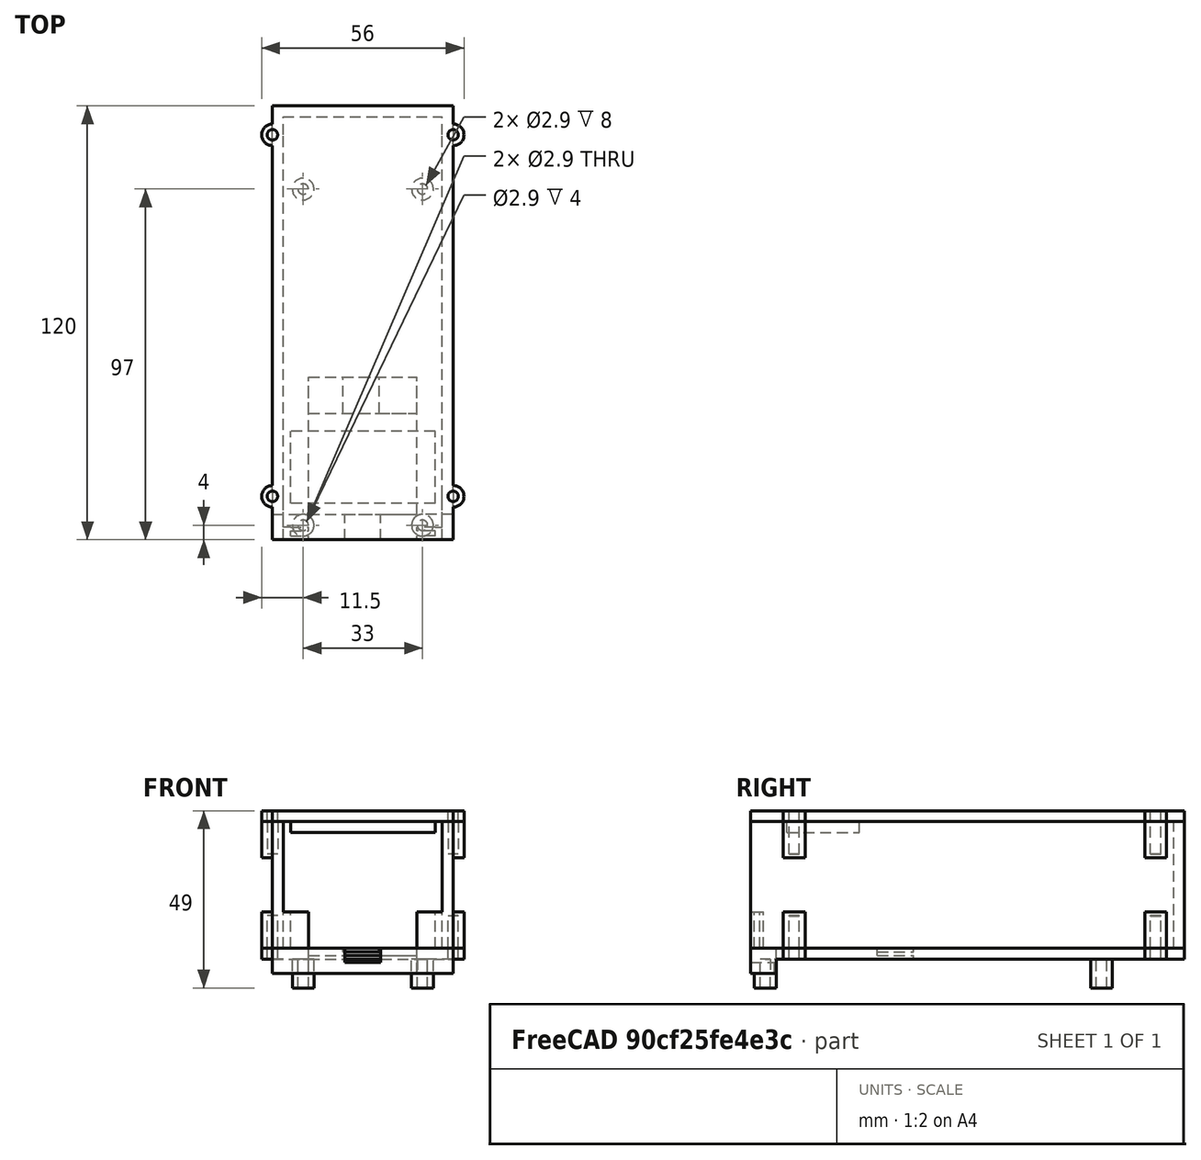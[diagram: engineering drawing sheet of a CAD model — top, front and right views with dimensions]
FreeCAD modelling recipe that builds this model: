
FCSTD DOCUMENT  (FreeCAD 0.18.4R)
Label: case
License: All rights reserved
LicenseURL: http://en.wikipedia.org/wiki/All_rights_reserved
objects: Part::FeaturePython×47, Part::Cylinder×29, Part::Box×18, Part::Mirroring×3
note: 97 computed .brp shape members not serialized (recipe doc carries the construction recipe); baked Part::Feature solids carry a one-line shape summary decoded from their .brp

FEATURE [Part::Box] Box002  label="Cube002"
  AttacherType = Attacher::AttachEngine3D
  Height = 10
  Length = 5
  Placement = pos=(0,2.5,1) rot=(0,0,1;0rad)
  Width = 1
FEATURE [Part::Mirroring] Part__Mirroring  label="Cube003 (Mirror #1)"
  Base = (0,0,0)
  Normal = (1,0,0)
FEATURE [Part::Mirroring] Part__Mirroring001  label="Cube004 (Mirror #2)"
  Base = (0,0,0)
  Normal = (1,0,0)
FEATURE [Part::Mirroring] Part__Mirroring002  label="Cube005 (Mirror #3)"
  Base = (0,0,0)
  Normal = (1,0,0)
FEATURE [Part::Box] Box007  label="Cube007"
  AttacherType = Attacher::AttachEngine3D
  Height = 3
  Length = 10
  Placement = pos=(-5,0,-2) rot=(0,0,1;0rad)
  Width = 45
FEATURE [Part::Box] Box009  label="Cube009"
  AttacherType = Attacher::AttachEngine3D
  Height = 35
  Length = 44
  Placement = pos=(-2,117,1) rot=(0,0,1;0rad)
  Width = 3
FEATURE [Part::Box] Box016  label="Floor"
  AttacherType = Attacher::AttachEngine3D
  Height = 3
  Length = 50
  Placement = pos=(-5,45,-2) rot=(0,0,1;0rad)
  Width = 75
FEATURE [Part::Box] Box018  label="Cube016"
  AttacherType = Attacher::AttachEngine3D
  Height = 1
  Length = 10
  Placement = pos=(14.5,35,0) rot=(0,0,1;0rad)
  Width = 10
FEATURE [Part::Box] Box008  label="Cube008"
  AttacherType = Attacher::AttachEngine3D
  Height = 2
  Length = 30
  Placement = pos=(5,35,-1) rot=(0,0,1;0rad)
  Width = 10
FEATURE [Part::FeaturePython] Cutout005  # WARN: FeaturePython — macro-defined, semantics opaque (R4)
  Base = -> Box008
  Tolerance = 0
  Tool = -> Box018
FEATURE [Part::Box] Box  label="Cube"
  AttacherType = Attacher::AttachEngine3D
  Height = 10
  Length = 5
  Placement = pos=(0,0,1) rot=(0,0,1;0rad)
  Width = 1
FEATURE [Part::Box] Box001  label="Cube001"
  AttacherType = Attacher::AttachEngine3D
  Height = 10
  Length = 3.5
  Placement = pos=(-2e-16,0,1) rot=(0,0,1;1.5708rad)
  Width = 2
FEATURE [Part::Box] Box010  label="Cube010"
  AttacherType = Attacher::AttachEngine3D
  Height = 35
  Length = 3
  Placement = pos=(-5,0,1) rot=(0,0,1;0rad)
  Width = 120
FEATURE [Part::Box] Box020  label="Cube018"
  AttacherType = Attacher::AttachEngine3D
  Height = 3
  Length = 10
  Placement = pos=(45,-1e-14,34) rot=(0,0,1;1.5708rad)
  Width = 50
FEATURE [Part::Box] Box021  label="Cube019"
  AttacherType = Attacher::AttachEngine3D
  Height = 3
  Length = 20
  Placement = pos=(45,10,34) rot=(0,0,1;1.5708rad)
  Width = 50
FEATURE [Part::Box] Box022  label="Cube020"
  AttacherType = Attacher::AttachEngine3D
  Height = 3
  Length = 20
  Placement = pos=(40,10,31) rot=(0,0,1;1.5708rad)
  Width = 40
FEATURE [Part::Box] Box023  label="Cube021"
  AttacherType = Attacher::AttachEngine3D
  Height = 3
  Length = 90
  Placement = pos=(45,30,34) rot=(0,0,1;1.5708rad)
  Width = 50
FEATURE [Part::FeaturePython] Connect  # WARN: FeaturePython — macro-defined, semantics opaque (R4)
  Objects = -> [Part__Mirroring,Part__Mirroring002,Part__Mirroring001]
  Placement = pos=(40,0,1) rot=(0,0,1;0rad)
  Tolerance = 0
FEATURE [Part::Box] Box019  label="Cube017"
  AttacherType = Attacher::AttachEngine3D
  Height = 35
  Length = 3
  Placement = pos=(42,0,1) rot=(0,0,1;0rad)
  Width = 120
FEATURE [Part::Box] Box031  label="Cube028"
  AttacherType = Attacher::AttachEngine3D
  Height = 7
  Length = 30
  Placement = pos=(5,0,-6) rot=(0,0,1;0rad)
  Width = 7
FEATURE [Part::Box] Box032  label="Cube029"
  AttacherType = Attacher::AttachEngine3D
  Height = 4
  Length = 10
  Placement = pos=(15,0,-3) rot=(0,0,1;0rad)
  Width = 7
FEATURE [Part::Cylinder] Cylinder036  label="outer016"
  Angle = 360
  AttacherType = Attacher::AttachEngine3D
  Height = 3
  Placement = pos=(-69,17,-9) rot=(0,0,1;0rad)
  Radius = 3
FEATURE [Part::Cylinder] Cylinder038  label="M3 cutout021"
  Angle = 360
  AttacherType = Attacher::AttachEngine3D
  Height = 3
  Placement = pos=(-69,17,-9) rot=(0,0,1;0rad)
  Radius = 1.45
FEATURE [Part::FeaturePython] Cutout007  # WARN: FeaturePython — macro-defined, semantics opaque (R4)
  Base = -> Cylinder036
  Placement = pos=(64,95,7) rot=(0,0,1;0rad)
  Tolerance = 0
  Tool = -> Cylinder038
FEATURE [Part::FeaturePython] Cutout008  # WARN: FeaturePython — macro-defined, semantics opaque (R4)
  Placement = pos=(64,95,26) rot=(0,0,1;0rad)
  Tolerance = 0
FEATURE [Part::FeaturePython] Cutout011  # WARN: FeaturePython — macro-defined, semantics opaque (R4)
  Placement = pos=(114,95,7) rot=(0,0,1;0rad)
  Tolerance = 0
FEATURE [Part::Cylinder] Cylinder051  label="M3 cutout029"
  Angle = 360
  AttacherType = Attacher::AttachEngine3D
  Height = 10
  Placement = pos=(5,94,-10) rot=(0,0,1;0rad)
  Radius = 1.45
FEATURE [Part::Cylinder] Cylinder052  label="outer023"
  Angle = 360
  AttacherType = Attacher::AttachEngine3D
  Height = 10
  Placement = pos=(5,94,-10) rot=(0,0,1;0rad)
  Radius = 3
FEATURE [Part::FeaturePython] Cutout012  label="Batter holder screw 1"  # WARN: FeaturePython — macro-defined, semantics opaque (R4)
  Base = -> Cylinder052
  Placement = pos=(-1.5,3,0) rot=(0,0,1;0rad)
  Tolerance = 0
  Tool = -> Cylinder051
FEATURE [Part::Cylinder] Cylinder053  label="M3 cutout030"
  Angle = 360
  AttacherType = Attacher::AttachEngine3D
  Height = 10
  Placement = pos=(5,94,-10) rot=(0,0,1;0rad)
  Radius = 1.45
FEATURE [Part::Cylinder] Cylinder054  label="outer024"
  Angle = 360
  AttacherType = Attacher::AttachEngine3D
  Height = 10
  Placement = pos=(5,94,-10) rot=(0,0,1;0rad)
  Radius = 3
FEATURE [Part::FeaturePython] Cutout013  label="Batter holder screw 2"  # WARN: FeaturePython — macro-defined, semantics opaque (R4)
  Base = -> Cylinder054
  Placement = pos=(31.5,3,0) rot=(0,0,1;0rad)
  Tolerance = 0
  Tool = -> Cylinder053
FEATURE [Part::Cylinder] Cylinder055  label="M3 cutout031"
  Angle = 360
  AttacherType = Attacher::AttachEngine3D
  Height = 10
  Placement = pos=(5,94,-10) rot=(0,0,1;0rad)
  Radius = 1.45
FEATURE [Part::Cylinder] Cylinder056  label="outer025"
  Angle = 360
  AttacherType = Attacher::AttachEngine3D
  Height = 10
  Placement = pos=(5,94,-10) rot=(0,0,1;0rad)
  Radius = 3
FEATURE [Part::FeaturePython] Cutout014  label="Batter holder screw 3"  # WARN: FeaturePython — macro-defined, semantics opaque (R4)
  Base = -> Cylinder056
  Placement = pos=(31.5,-90,0) rot=(0,0,1;0rad)
  Tolerance = 0
  Tool = -> Cylinder055
FEATURE [Part::Cylinder] Cylinder058  label="outer026"
  Angle = 360
  AttacherType = Attacher::AttachEngine3D
  Height = 10
  Placement = pos=(5,94,-10) rot=(0,0,1;0rad)
  Radius = 3
FEATURE [Part::Cylinder] Cylinder059  label="M3 cutout033"
  Angle = 360
  AttacherType = Attacher::AttachEngine3D
  Height = 10
  Placement = pos=(5,94,-10) rot=(0,0,1;0rad)
  Radius = 1.45
FEATURE [Part::FeaturePython] Cutout018  label="Batter holder screw 004"  # WARN: FeaturePython — macro-defined, semantics opaque (R4)
  Base = -> Cylinder058
  Placement = pos=(-1.5,-90,0) rot=(0,0,1;0rad)
  Tolerance = 0
  Tool = -> Cylinder059
FEATURE [Part::Box] Box006  label="Cube006"
  AttacherType = Attacher::AttachEngine3D
  Height = 3
  Length = 10
  Placement = pos=(35,0,-2) rot=(0,0,1;0rad)
  Width = 45
FEATURE [Part::Cylinder] Cylinder060  label="M3 cutout034"
  Angle = 360
  AttacherType = Attacher::AttachEngine3D
  Height = 12
  Placement = pos=(-5,112,-2) rot=(0,0,1;0rad)
  Radius = 1.45
FEATURE [Part::FeaturePython] Cutout019  # WARN: FeaturePython — macro-defined, semantics opaque (R4)
  Base = -> Box016
  Tolerance = 0
  Tool = -> Cylinder060
FEATURE [Part::FeaturePython] Cutout020  # WARN: FeaturePython — macro-defined, semantics opaque (R4)
  Base = -> Box010
  Tolerance = 0
  Tool = -> Cylinder060
FEATURE [Part::Cylinder] Cylinder061  label="M3 cutout035"
  Angle = 360
  AttacherType = Attacher::AttachEngine3D
  Height = 12
  Placement = pos=(45,112,-2) rot=(0,0,1;0rad)
  Radius = 1.45
FEATURE [Part::FeaturePython] Cutout021  # WARN: FeaturePython — macro-defined, semantics opaque (R4)
  Base = -> Box019
  Tolerance = 0
  Tool = -> Cylinder061
FEATURE [Part::FeaturePython] Cutout022  # WARN: FeaturePython — macro-defined, semantics opaque (R4)
  Base = -> Cutout019
  Tolerance = 0
  Tool = -> Cylinder061
FEATURE [Part::Cylinder] Cylinder062  label="M3 cutout036"
  Angle = 360
  AttacherType = Attacher::AttachEngine3D
  Height = 1
  Placement = pos=(-5,112,10) rot=(0,0,1;0rad)
  Radius = 1.45
FEATURE [Part::Cylinder] Cylinder064  label="outer027"
  Angle = 360
  AttacherType = Attacher::AttachEngine3D
  Height = 3
  Placement = pos=(-69,17,-9) rot=(0,0,1;0rad)
  Radius = 3
FEATURE [Part::Cylinder] Cylinder065  label="M3 cutout038"
  Angle = 360
  AttacherType = Attacher::AttachEngine3D
  Height = 3
  Placement = pos=(-69,17,-9) rot=(0,0,1;0rad)
  Radius = 1.45
FEATURE [Part::FeaturePython] Cutout024  # WARN: FeaturePython — macro-defined, semantics opaque (R4)
  Base = -> Cylinder064
  Placement = pos=(64,-5,7) rot=(0,0,1;0rad)
  Tolerance = 0
  Tool = -> Cylinder065
FEATURE [Part::Cylinder] Cylinder067  label="M3 cutout039"
  Angle = 360
  AttacherType = Attacher::AttachEngine3D
  Height = 12
  Placement = pos=(-5,12,-2) rot=(0,0,1;0rad)
  Radius = 1.45
FEATURE [Part::FeaturePython] Cutout025  # WARN: FeaturePython — macro-defined, semantics opaque (R4)
  Base = -> Box007
  Tolerance = 0
  Tool = -> Cylinder067
FEATURE [Part::FeaturePython] Cutout026  # WARN: FeaturePython — macro-defined, semantics opaque (R4)
  Base = -> Cutout020
  Tolerance = 0
  Tool = -> Cylinder067
FEATURE [Part::FeaturePython] Cutout027  # WARN: FeaturePython — macro-defined, semantics opaque (R4)
  Placement = pos=(114,-5,7) rot=(0,0,1;0rad)
  Tolerance = 0
FEATURE [Part::Cylinder] Cylinder073  label="M3 cutout043"
  Angle = 360
  AttacherType = Attacher::AttachEngine3D
  Height = 12
  Placement = pos=(45,12,-2) rot=(0,0,1;0rad)
  Radius = 1.45
FEATURE [Part::FeaturePython] Cutout029  # WARN: FeaturePython — macro-defined, semantics opaque (R4)
  Base = -> Cutout021
  Tolerance = 0
  Tool = -> Cylinder073
FEATURE [Part::FeaturePython] Cutout030  # WARN: FeaturePython — macro-defined, semantics opaque (R4)
  Base = -> Box006
  Tolerance = 0
  Tool = -> Cylinder073
FEATURE [Part::FeaturePython] Cutout  # WARN: FeaturePython — macro-defined, semantics opaque (R4)
  Base = -> Box031
  Tolerance = 0
  Tool = -> Box032
FEATURE [Part::FeaturePython] Cutout015  # WARN: FeaturePython — macro-defined, semantics opaque (R4)
  Base = -> Cutout
  Tolerance = 0
  Tool = -> Cylinder055
FEATURE [Part::Box] Box033  label="Cube030"
  AttacherType = Attacher::AttachEngine3D
  Height = 4
  Length = 10
  Placement = pos=(-5,0,-6) rot=(0,0,1;0rad)
  Width = 7
FEATURE [Part::Cylinder] Cylinder074  label="M3 cutout044"
  Angle = 360
  AttacherType = Attacher::AttachEngine3D
  Height = 10
  Placement = pos=(3.5,4,-10) rot=(0,0,1;0rad)
  Radius = 1.45
FEATURE [Part::FeaturePython] Cutout031  # WARN: FeaturePython — macro-defined, semantics opaque (R4)
  Base = -> Box033
  Tolerance = 0
  Tool = -> Cylinder074
FEATURE [Part::FeaturePython] Cutout032  # WARN: FeaturePython — macro-defined, semantics opaque (R4)
  Base = -> Box033
  Placement = pos=(40,1e-15,-8) rot=(0,1,0;3.14159rad)
  Tolerance = 0
  Tool = -> Cylinder074
FEATURE [Part::Cylinder] Cylinder076  label="M3 cutout046"
  Angle = 360
  AttacherType = Attacher::AttachEngine3D
  Height = 1
  Placement = pos=(44.9494,112,9.86308) rot=(0,0,1;0rad)
  Radius = 1.45
FEATURE [Part::Cylinder] Cylinder077  label="M3 cutout047"
  Angle = 360
  AttacherType = Attacher::AttachEngine3D
  Height = 1
  Placement = pos=(44.9494,12,9.86308) rot=(0,0,1;0rad)
  Radius = 1.45
FEATURE [Part::FeaturePython] Connect006  # WARN: FeaturePython — macro-defined, semantics opaque (R4)
  Objects = -> [Cutout008,Cylinder062]
  Placement = pos=(0,-100,0) rot=(0,0,1;0rad)
  Tolerance = 0
FEATURE [Part::FeaturePython] Connect007  # WARN: FeaturePython — macro-defined, semantics opaque (R4)
  Objects = -> [Cutout008,Cylinder062]
  Placement = pos=(50,0,0) rot=(0,0,1;0rad)
  Tolerance = 0
FEATURE [Part::FeaturePython] Connect008  # WARN: FeaturePython — macro-defined, semantics opaque (R4)
  Objects = -> [Cutout008,Cylinder062]
  Placement = pos=(50,-100,0) rot=(0,0,1;0rad)
  Tolerance = 0
FEATURE [Part::FeaturePython] Connect009  # WARN: FeaturePython — macro-defined, semantics opaque (R4)
  Objects = -> [Cutout008,Cylinder062]
  Placement = pos=(50,124,37) rot=(1,0,0;3.14159rad)
  Tolerance = 0
FEATURE [Part::Cylinder] Cylinder078  label="M3 cutout048"
  Angle = 360
  AttacherType = Attacher::AttachEngine3D
  Height = 10
  Placement = pos=(45,12,26) rot=(0,0,1;0rad)
  Radius = 1.45
FEATURE [Part::FeaturePython] Cutout033  # WARN: FeaturePython — macro-defined, semantics opaque (R4)
  Base = -> Cutout029
  Tolerance = 0
  Tool = -> Cylinder078
FEATURE [Part::FeaturePython] Connect011  # WARN: FeaturePython — macro-defined, semantics opaque (R4)
  Objects = -> [Cutout008,Cylinder062]
  Placement = pos=(50,224,37) rot=(1,0,0;3.14159rad)
  Tolerance = 0
FEATURE [Part::Cylinder] Cylinder079  label="M3 cutout049"
  Angle = 360
  AttacherType = Attacher::AttachEngine3D
  Height = 10
  Placement = pos=(45,112,26) rot=(0,0,1;0rad)
  Radius = 1.45
FEATURE [Part::FeaturePython] Cutout034  # WARN: FeaturePython — macro-defined, semantics opaque (R4)
  Base = -> Cutout033
  Tolerance = 0
  Tool = -> Cylinder079
FEATURE [Part::FeaturePython] Cutout035  # WARN: FeaturePython — macro-defined, semantics opaque (R4)
  Placement = pos=(64,95,26) rot=(0,0,1;0rad)
  Tolerance = 0
FEATURE [Part::Cylinder] Cylinder080  label="M3 cutout050"
  Angle = 360
  AttacherType = Attacher::AttachEngine3D
  Height = 1
  Placement = pos=(-5,112,10) rot=(0,0,1;0rad)
  Radius = 1.45
FEATURE [Part::Cylinder] Cylinder081  label="M3 cutout051"
  Angle = 360
  AttacherType = Attacher::AttachEngine3D
  Height = 10
  Placement = pos=(-5,112,26) rot=(0,0,1;0rad)
  Radius = 1.45
FEATURE [Part::FeaturePython] Cutout036  # WARN: FeaturePython — macro-defined, semantics opaque (R4)
  Base = -> Cutout026
  Tolerance = 0
  Tool = -> Cylinder081
FEATURE [Part::FeaturePython] Connect013  # WARN: FeaturePython — macro-defined, semantics opaque (R4)
  Objects = -> [Cutout008,Cylinder062]
  Placement = pos=(0,124,37) rot=(1,0,0;3.14159rad)
  Tolerance = 0
FEATURE [Part::Cylinder] Cylinder082  label="M3 cutout052"
  Angle = 360
  AttacherType = Attacher::AttachEngine3D
  Height = 10
  Placement = pos=(-5,12,26) rot=(0,0,1;0rad)
  Radius = 1.45
FEATURE [Part::FeaturePython] Cutout037  # WARN: FeaturePython — macro-defined, semantics opaque (R4)
  Base = -> Cutout036
  Tolerance = 0
  Tool = -> Cylinder082
FEATURE [Part::FeaturePython] Connect012  # WARN: FeaturePython — macro-defined, semantics opaque (R4)
  Objects = -> [Cutout035,Cylinder080]
  Placement = pos=(0,224,37) rot=(1,0,0;3.14159rad)
  Tolerance = 0
FEATURE [Part::FeaturePython] Connect005  # WARN: FeaturePython — macro-defined, semantics opaque (R4)
  Objects = -> [Cutout008,Cylinder062]
  Tolerance = 0
FEATURE [Part::FeaturePython] Connect015  label="Floor001"  # WARN: FeaturePython — macro-defined, semantics opaque (R4)
  Objects = -> [Cutout022,Cutout011,Cutout013,Cutout012,Cutout007,Cutout030,Cutout027,Cutout032,Cutout014,Cutout015,Cutout018,Cutout031,Cutout025,Cutout024,Cutout005]
  Placement = pos=(0,0,-8) rot=(0,0,1;0rad)
  Tolerance = 0
FEATURE [Part::FeaturePython] Cutout038  # WARN: FeaturePython — macro-defined, semantics opaque (R4)
  Base = -> Cylinder064
  Placement = pos=(64,-5,43) rot=(0,0,1;0rad)
  Tolerance = 0
  Tool = -> Cylinder065
FEATURE [Part::Cylinder] Cylinder083  label="M3 cutout053"
  Angle = 360
  AttacherType = Attacher::AttachEngine3D
  Height = 3
  Placement = pos=(-5,12,34) rot=(0,0,1;0rad)
  Radius = 1.45
FEATURE [Part::FeaturePython] Cutout039  # WARN: FeaturePython — macro-defined, semantics opaque (R4)
  Base = -> Box021
  Tolerance = 0
  Tool = -> Cylinder083
FEATURE [Part::FeaturePython] Connect014  label="Walls"  # WARN: FeaturePython — macro-defined, semantics opaque (R4)
  Objects = -> [Cylinder076,Connect012,Connect011,Connect007,Connect005,Cutout037,Connect006,Connect008,Connect013,Cylinder077,Cutout034,Connect009,Connect,Box001,Box002,Box009,Box]
  Placement = pos=(0,0,-8) rot=(0,0,1;0rad)
  Tolerance = 0
FEATURE [Part::FeaturePython] Cutout040  # WARN: FeaturePython — macro-defined, semantics opaque (R4)
  Base = -> Cylinder064
  Placement = pos=(114,-5,43) rot=(0,0,1;0rad)
  Tolerance = 0
  Tool = -> Cylinder065
FEATURE [Part::Cylinder] Cylinder084  label="M3 cutout054"
  Angle = 360
  AttacherType = Attacher::AttachEngine3D
  Height = 3
  Placement = pos=(45,12,34) rot=(0,0,1;0rad)
  Radius = 1.45
FEATURE [Part::FeaturePython] Cutout041  # WARN: FeaturePython — macro-defined, semantics opaque (R4)
  Base = -> Cutout039
  Tolerance = 0
  Tool = -> Cylinder084
FEATURE [Part::FeaturePython] Cutout042  # WARN: FeaturePython — macro-defined, semantics opaque (R4)
  Base = -> Cylinder064
  Placement = pos=(114,95,43) rot=(0,0,1;0rad)
  Tolerance = 0
  Tool = -> Cylinder065
FEATURE [Part::Cylinder] Cylinder085  label="M3 cutout055"
  Angle = 360
  AttacherType = Attacher::AttachEngine3D
  Height = 3
  Placement = pos=(45,112,34) rot=(0,0,1;0rad)
  Radius = 1.45
FEATURE [Part::FeaturePython] Cutout043  # WARN: FeaturePython — macro-defined, semantics opaque (R4)
  Base = -> Box023
  Tolerance = 0
  Tool = -> Cylinder085
FEATURE [Part::FeaturePython] Cutout044  # WARN: FeaturePython — macro-defined, semantics opaque (R4)
  Base = -> Cylinder064
  Placement = pos=(64,95,43) rot=(0,0,1;0rad)
  Tolerance = 0
  Tool = -> Cylinder065
FEATURE [Part::Cylinder] Cylinder086  label="M3 cutout056"
  Angle = 360
  AttacherType = Attacher::AttachEngine3D
  Height = 3
  Placement = pos=(-5,112,34) rot=(0,0,1;0rad)
  Radius = 1.45
FEATURE [Part::FeaturePython] Cutout045  # WARN: FeaturePython — macro-defined, semantics opaque (R4)
  Base = -> Cutout043
  Tolerance = 0
  Tool = -> Cylinder086
FEATURE [Part::FeaturePython] Connect016  label="lid"  # WARN: FeaturePython — macro-defined, semantics opaque (R4)
  Objects = -> [Box020,Box022,Cutout040,Cutout041,Cutout045,Cutout044,Cutout042,Cutout038]
  Placement = pos=(0,0,-6) rot=(0,0,1;0rad)
  Tolerance = 0
